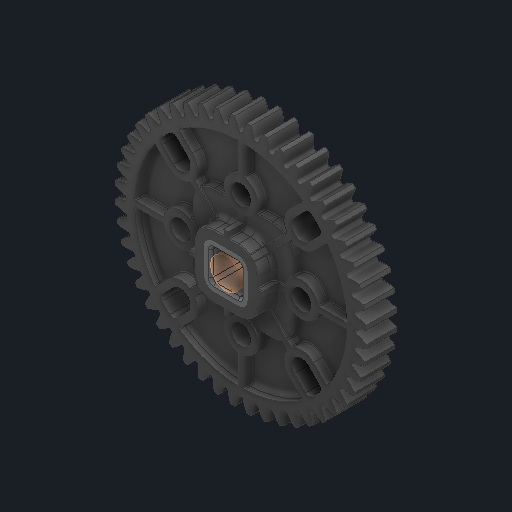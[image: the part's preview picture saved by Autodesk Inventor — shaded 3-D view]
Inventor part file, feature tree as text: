
AUTODESK INVENTOR PART (.ipt)
format: ipt  version: 2025 (Build 290162000, 162)  size: 3,926,016 bytes
history: native  units: in
note: dims shown in document units (in); Inventor stores cm internally (conversion verified against a paired STEP export)
features: other x6, sketch x3
ambient origin geometry x8: Origin, YZ Plane, XZ Plane, XY Plane, X Axis, Y Axis, Z Axis, Center Point
bodies: Solid1 (feature_tree), Solid2 (feature_tree)
feature tree (9):
  other  "Half Cut HS 48T Gear, No Insert.ipt"
  other  "Solid1::Half Cut HS 48T Gear, No Insert.ipt"
  other  "Solid2::Half Cut HS 48T Gear, No Insert.ipt"
  other  "TaggingFeature1"
  sketch  "Sketch1"  dims[d0=0.3937in]
  sketch  "Sketch2"
  sketch  "Sketch3"
  other  "Srf1"
  other  "Srf1::Derived"
